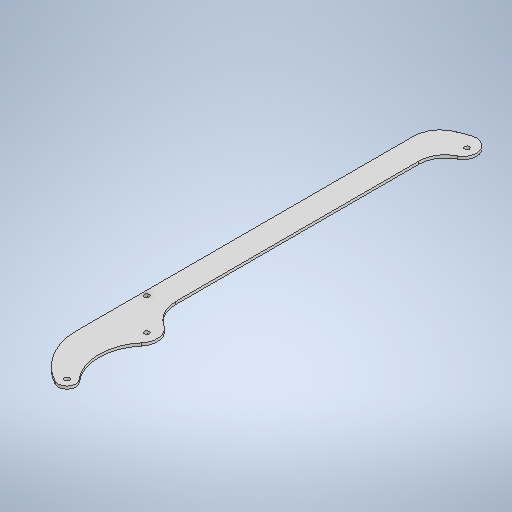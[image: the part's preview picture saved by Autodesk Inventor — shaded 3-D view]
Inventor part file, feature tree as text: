
AUTODESK INVENTOR PART (.ipt)
format: ipt  version: 2025.2 (Build 292293000, 293)  size: 289,280 bytes
history: native  units: in
note: dims shown in document units (in); Inventor stores cm internally (conversion verified against a paired STEP export)
features: extrude x2, sketch x2
ambient origin geometry x8: Origin, YZ Plane, XZ Plane, XY Plane, X Axis, Y Axis, Z Axis, Center Point
bodies: Solid1 (feature_tree)
feature tree (4):
  extrude  "Extrusion1"  Depth=1.9685in
  extrude  "Extrusion2"  Depth=0.0669in TaperAngle=0.0deg
  sketch  "Sketch1"  dims[d0=0.4291in d1=1.9685in]
  sketch  "Sketch2"  dims[d4=7.874in d5=0.0669in d6=0.0in d7=0.1181in d8=0.1181in d9=0.7874in d10=0.7874in d11=0.1181in d12=0.1181in d13=0.0669in d14=0.0in]
